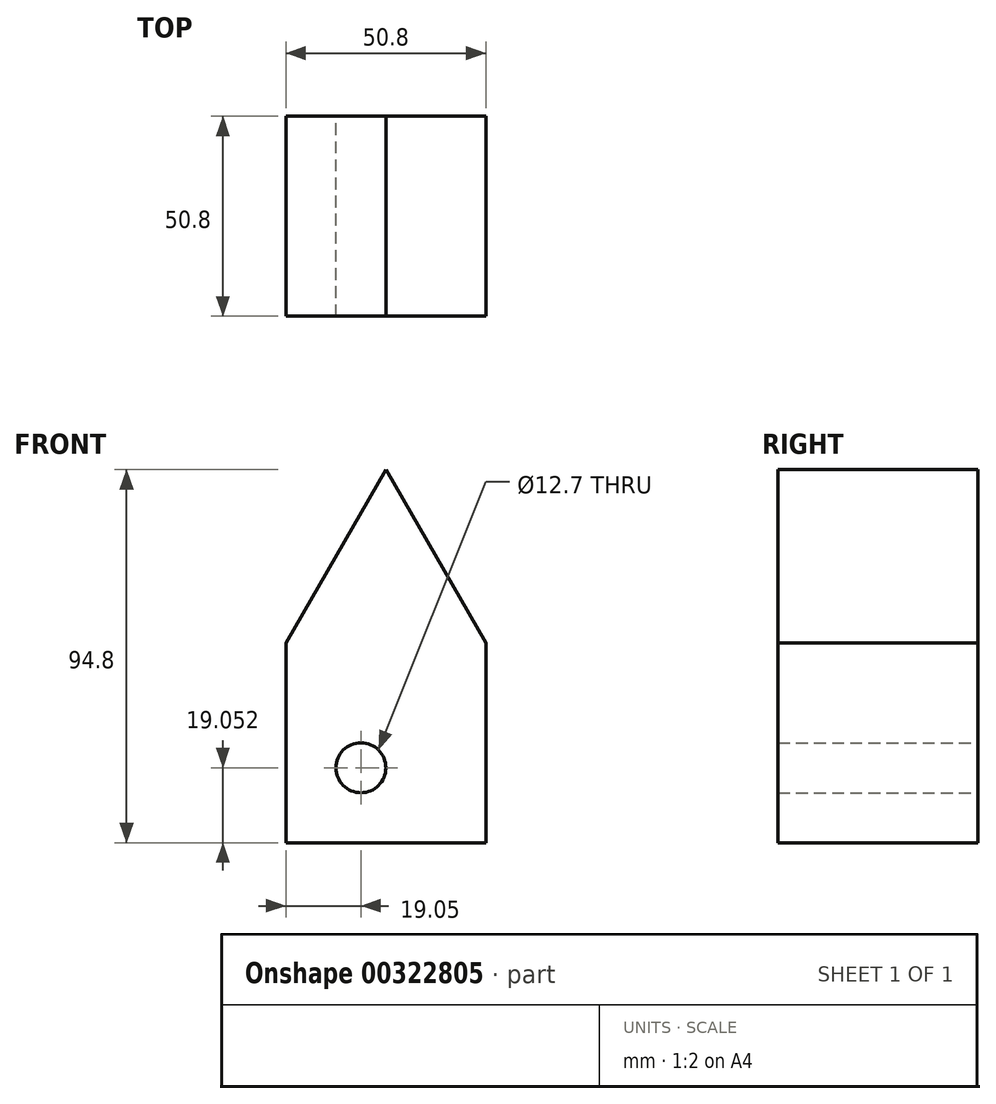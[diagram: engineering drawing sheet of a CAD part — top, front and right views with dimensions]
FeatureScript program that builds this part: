
annotation { "Feature Type Name" : "Feature", "Feature Type Description" : "" }
export const myFeature = defineFeature(function(context is Context, id is Id, definition is map)
    precondition{}
    {
        {
            var Q0;
            Q0=qCreatedBy(makeId("Front.planeOp"),FACE);
            var sketch = newSketch(context, id + "F0", { "sketchPlane" : qUnion([Q0])});
            skLineSegment(sketch, "E0.top", {"start": v(-25.4, -33.53) * mm, "end": v(25.4, -33.53) * mm});
            skLineSegment(sketch, "E0.left", {"start": v(-25.4, 17.27) * mm, "end": v(-25.4, -33.53) * mm});
            skLineSegment(sketch, "E0.right", {"start": v(25.4, 17.27) * mm, "end": v(25.4, -33.53) * mm});
            skLineSegment(sketch, "E1", {"start": v(-25.4, 17.27) * mm, "end": v(0, 61.27) * mm});
            skLineSegment(sketch, "E2", {"start": v(0, 61.27) * mm, "end": v(25.4, 17.27) * mm});
            skCircle(sketch, "E3", {"center": v(-6.35, -14.48) * mm, "radius": 6.35 * mm});
            skSolve(sketch);
        }
        {
            var Q0;
            Q0=makeQuery(id+"F0.imprint","IMPRINT",FACE,{"disambiguationData":[TD([[makeQuery(id+"F0.imprint","IMPRINT",EDGE,{"derivedFrom":sQuery(id+"F0.wireOp",EDGE,"E0.top")}),1.0]])]});
            extrude(context, id + "F1", {"entities" : qUnion([Q0]), "depth" : 50.8 * mm});
        }
    });
